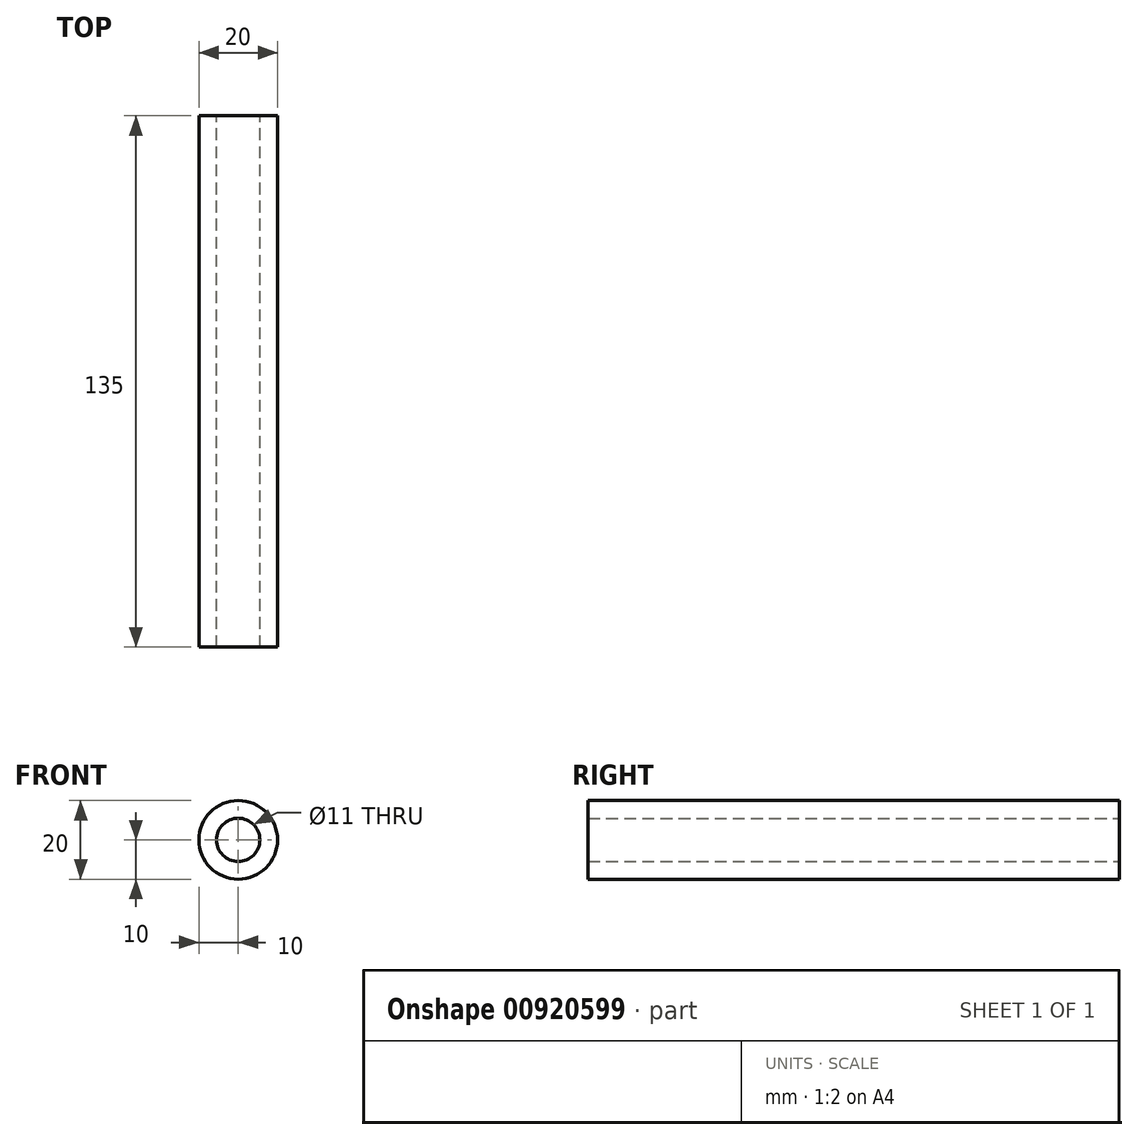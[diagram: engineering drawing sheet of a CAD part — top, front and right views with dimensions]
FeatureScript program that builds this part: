
annotation { "Feature Type Name" : "Feature", "Feature Type Description" : "" }
export const myFeature = defineFeature(function(context is Context, id is Id, definition is map)
    precondition{}
    {
        {
            var Q0;
            Q0=qCreatedBy(makeId("Front.planeOp"),FACE);
            var sketch = newSketch(context, id + "F0", { "sketchPlane" : qUnion([Q0])});
            skCircle(sketch, "E0", {"center": v(0, 0) * mm, "radius": 10 * mm});
            skCircle(sketch, "E1", {"center": v(0, 0) * mm, "radius": 5.5 * mm});
            skSolve(sketch);
        }
        {
            var Q0;
            Q0=makeQuery(id+"F0.imprint","IMPRINT",FACE,{"disambiguationData":[TD([[makeQuery(id+"F0.imprint","IMPRINT",EDGE,{"derivedFrom":sQuery(id+"F0.wireOp",EDGE,"E0")}),1.0]])]});
            extrude(context, id + "F1", {"entities" : qUnion([Q0]), "depth" : 135 * mm, "offsetDistance" : 25 * mm});
        }
    });
